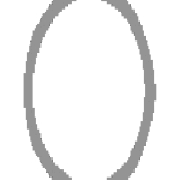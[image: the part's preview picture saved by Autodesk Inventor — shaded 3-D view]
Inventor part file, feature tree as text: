
AUTODESK INVENTOR PART (.ipt)
format: ipt  version: 2021 (Build 250183000, 183)  size: 112,128 bytes
history: native  units: in
note: dims shown in document units (in); Inventor stores cm internally (conversion verified against a paired STEP export)
features: other x4, sketch x3, plane x1
ambient origin geometry x8: Origin, YZ Plane, XZ Plane, XY Plane, X Axis, Y Axis, Z Axis, Center Point
bodies: Solid1 (feature_tree), Body (feature_tree)
feature tree (8):
  other  "Driven Length"
  other  "Frame Generator"
  other  "Start Plane"
  other  "End Plane"
  sketch  "Sketch"  dims[d2=14.6042in d4=-0.0in d5=14.6042in d6=0.12in d7=0.0in d8=90.0deg d9=14.6042in]
  sketch  "Sketch2"  dims[d0=1.0in]
  plane  "Work Plane3"
  sketch  "Sketch3"  dims[d1=0.065in]
